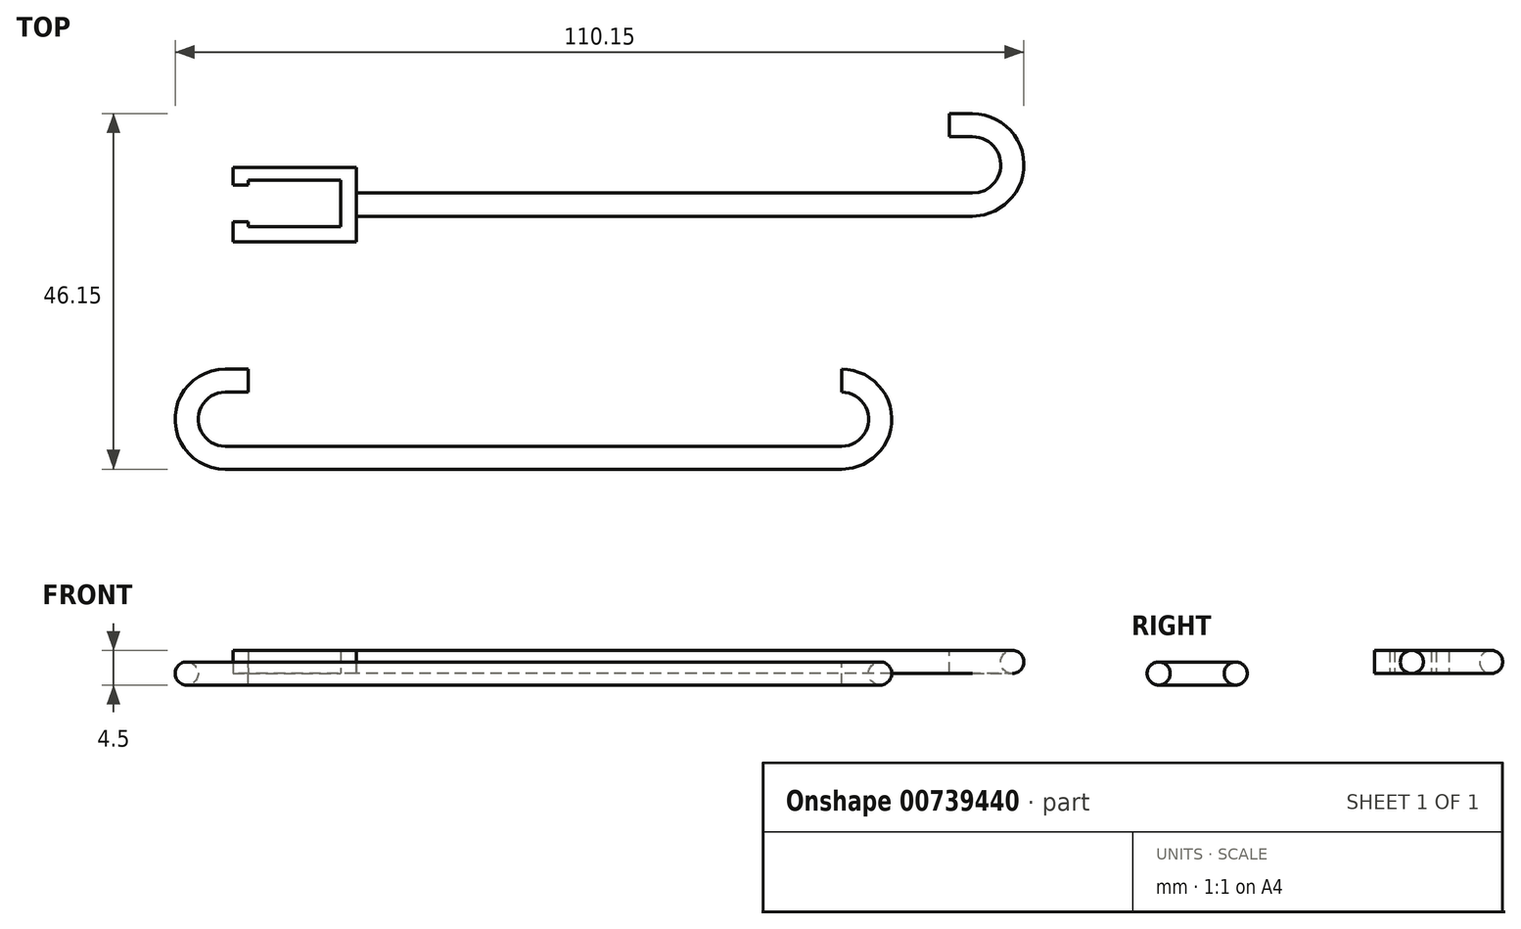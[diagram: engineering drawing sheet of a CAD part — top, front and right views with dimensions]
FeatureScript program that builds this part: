
annotation { "Feature Type Name" : "Feature", "Feature Type Description" : "" }
export const myFeature = defineFeature(function(context is Context, id is Id, definition is map)
    precondition{}
    {
        {
            var Q0;
            Q0=qCreatedBy(makeId("Top.planeOp"),FACE);
            var sketch = newSketch(context, id + "F0", { "sketchPlane" : qUnion([Q0])});
            skLineSegment(sketch, "E0", {"start": v(0, 0) * mm, "end": v(12, 0) * mm});
            skLineSegment(sketch, "E1", {"start": v(12, 0) * mm, "end": v(12, 6) * mm});
            skLineSegment(sketch, "E2", {"start": v(12, 6) * mm, "end": v(0, 6) * mm});
            skLineSegment(sketch, "E3", {"start": v(0, 6) * mm, "end": v(0, 5.4) * mm});
            skLineSegment(sketch, "E4", {"start": v(0, 5.4) * mm, "end": v(-2, 5.4) * mm});
            skLineSegment(sketch, "E5", {"start": v(-2, 5.4) * mm, "end": v(-2, 7.7) * mm});
            skLineSegment(sketch, "E6", {"start": v(-2, 7.7) * mm, "end": v(14, 7.7) * mm});
            skLineSegment(sketch, "E7", {"start": v(14, 7.7) * mm, "end": v(14, -2) * mm});
            skLineSegment(sketch, "E8", {"start": v(14, -2) * mm, "end": v(-2, -2) * mm});
            skLineSegment(sketch, "E9", {"start": v(-2, -2) * mm, "end": v(-2, 0.6) * mm});
            skLineSegment(sketch, "E10", {"start": v(-2, 0.6) * mm, "end": v(0, 0.6) * mm});
            skLineSegment(sketch, "E11", {"start": v(0, 0.6) * mm, "end": v(0, 0) * mm});
            skSolve(sketch);
        }
        {
            var Q0;
            Q0 = qSketchRegion(id + "F0", true);
            extrude(context, id + "F1", {"entities" : qUnion([Q0]), "depth" : 3 * mm, "offsetDistance" : 25 * mm});
        }
        {
            var Q0;
            Q0=makeQuery(id+"F1.opExtrude","SWEPT_FACE",FACE,{"disambiguationData":[OSD([sQuery(id+"F0.wireOp",EDGE,"E7")])]});
            var sketch = newSketch(context, id + "F2", { "sketchPlane" : qUnion([Q0])});
            skCircle(sketch, "E12", {"center": v(2.85, 1.5) * mm, "radius": 1.5 * mm});
            skPoint(sketch, "E12.centerSnap0", {"position": v(7.7, 1.5) * mm});
            skPoint(sketch, "E12.centerSnap1", {"position": v(2.85, 0) * mm});
            skSolve(sketch);
        }
        {
            var Q0;
            Q0 = qSketchRegion(id + "F2", true);
            extrude(context, id + "F3", {"entities" : qUnion([Q0]), "operationType" : NewBodyOperationType.ADD, "depth" : 80 * mm, "offsetDistance" : 25 * mm});
        }
        {
            var Q0;
            Q0=makeQuery(id+"F3.opExtrude","CAP_FACE",FACE,{"disambiguationData":[OSD([sQuery(id+"F2.wireOp",EDGE,"E12")])],"isStart":false});
            var sketch = newSketch(context, id + "F4", { "sketchPlane" : qUnion([Q0])});
            skCircle(sketch, "E13", {"center": v(2.85, 1.5) * mm, "radius": 1.5 * mm});
            skSolve(sketch);
        }
        {
            var Q0;
            Q0=qCreatedBy(makeId("Top.planeOp"),FACE);
            cPlane(context, id + "F5", {"entities" : qUnion([Q0]), "cplaneType" : CPlaneType.OFFSET, "offset" : 1.5 * mm, "width" : 150 * mm, "height" : 150 * mm});
        }
        {
            var Q0;
            Q0=qCreatedBy(id+"F5.planeOp",FACE);
            var sketch = newSketch(context, id + "F6", { "sketchPlane" : qUnion([Q0])});
            skLineSegment(sketch, "E14", {"start": v(0, 0) * mm, "end": v(94, 0) * mm, "construction": true});
            skLineSegment(sketch, "E15", {"start": v(94, 0) * mm, "end": v(94, 3) * mm, "construction": true});
            skLineSegment(sketch, "E16", {"start": v(94, 3) * mm, "end": v(94, 8) * mm, "construction": true});
            skArc(sketch, "E17", {"start": v(94, 3) * mm, "mid": v(99, 8) * mm, "end": v(94, 13) * mm});
            skLineSegment(sketch, "E18", {"start": v(94, 13) * mm, "end": v(91, 13) * mm});
            skSolve(sketch);
        }
        {
            var Q0;
            Q0 = qSketchRegion(id + "F4", true);
            var Q1;
            Q1 = qConstructionFilter(qBodyType(qCreatedBy(id + "F6" ,EDGE), BodyType.WIRE), ConstructionObject.NO);
            sweep(context, id + "F7", {"operationType" : NewBodyOperationType.ADD, "profiles" : qUnion([Q0]), "path" : qUnion([Q1])});
        }
        {
            var Q0;
            Q0=qCreatedBy(makeId("Top.planeOp"),FACE);
            var sketch = newSketch(context, id + "F8", { "sketchPlane" : qUnion([Q0])});
            skLineSegment(sketch, "E19", {"start": v(0, 0) * mm, "end": v(0, -20) * mm, "construction": true});
            skLineSegment(sketch, "E20", {"start": v(0, -20) * mm, "end": v(-3, -20) * mm});
            skLineSegment(sketch, "E21", {"start": v(0, -20) * mm, "end": v(0, -25) * mm, "construction": true});
            skLineSegment(sketch, "E22", {"start": v(0, -25) * mm, "end": v(-3, -25) * mm, "construction": true});
            skArc(sketch, "E23", {"start": v(-3, -20) * mm, "mid": v(-8, -25) * mm, "end": v(-3, -30) * mm});
            skLineSegment(sketch, "E24", {"start": v(-3, -30) * mm, "end": v(77, -30) * mm});
            skLineSegment(sketch, "E25", {"start": v(77, -30) * mm, "end": v(77, -25) * mm, "construction": true});
            skArc(sketch, "E26", {"start": v(77, -30) * mm, "mid": v(82, -25) * mm, "end": v(77, -20) * mm});
            skSolve(sketch);
        }
        {
            var Q0;
            Q0=qCreatedBy(makeId("Right.planeOp"),FACE);
            var sketch = newSketch(context, id + "F9", { "sketchPlane" : qUnion([Q0])});
            skPoint(sketch, "E27.0", {"position": v(-20, 0) * mm});
            skCircle(sketch, "E28", {"center": v(-20, 0) * mm, "radius": 1.5 * mm});
            skSolve(sketch);
        }
        {
            var Q0;
            Q0 = qSketchRegion(id + "F9", true);
            var Q1;
            Q1 = qConstructionFilter(qBodyType(qCreatedBy(id + "F9" ,EDGE), BodyType.WIRE), ConstructionObject.NO);
            extrude(context, id + "F10", {"entities" : qUnion([Q0]), "surfaceEntities" : qUnion([Q1]), "oppositeDirection" : true, "depth" : 3 * mm, "offsetDistance" : 25 * mm});
        }
        {
            var Q0;
            Q0 = qSketchRegion(id + "F9", true);
            var Q1;
            Q1 = qConstructionFilter(qBodyType(qCreatedBy(id + "F8" ,EDGE), BodyType.WIRE), ConstructionObject.NO);
            sweep(context, id + "F11", {"operationType" : NewBodyOperationType.ADD, "profiles" : qUnion([Q0]), "path" : qUnion([Q1])});
        }
    });
